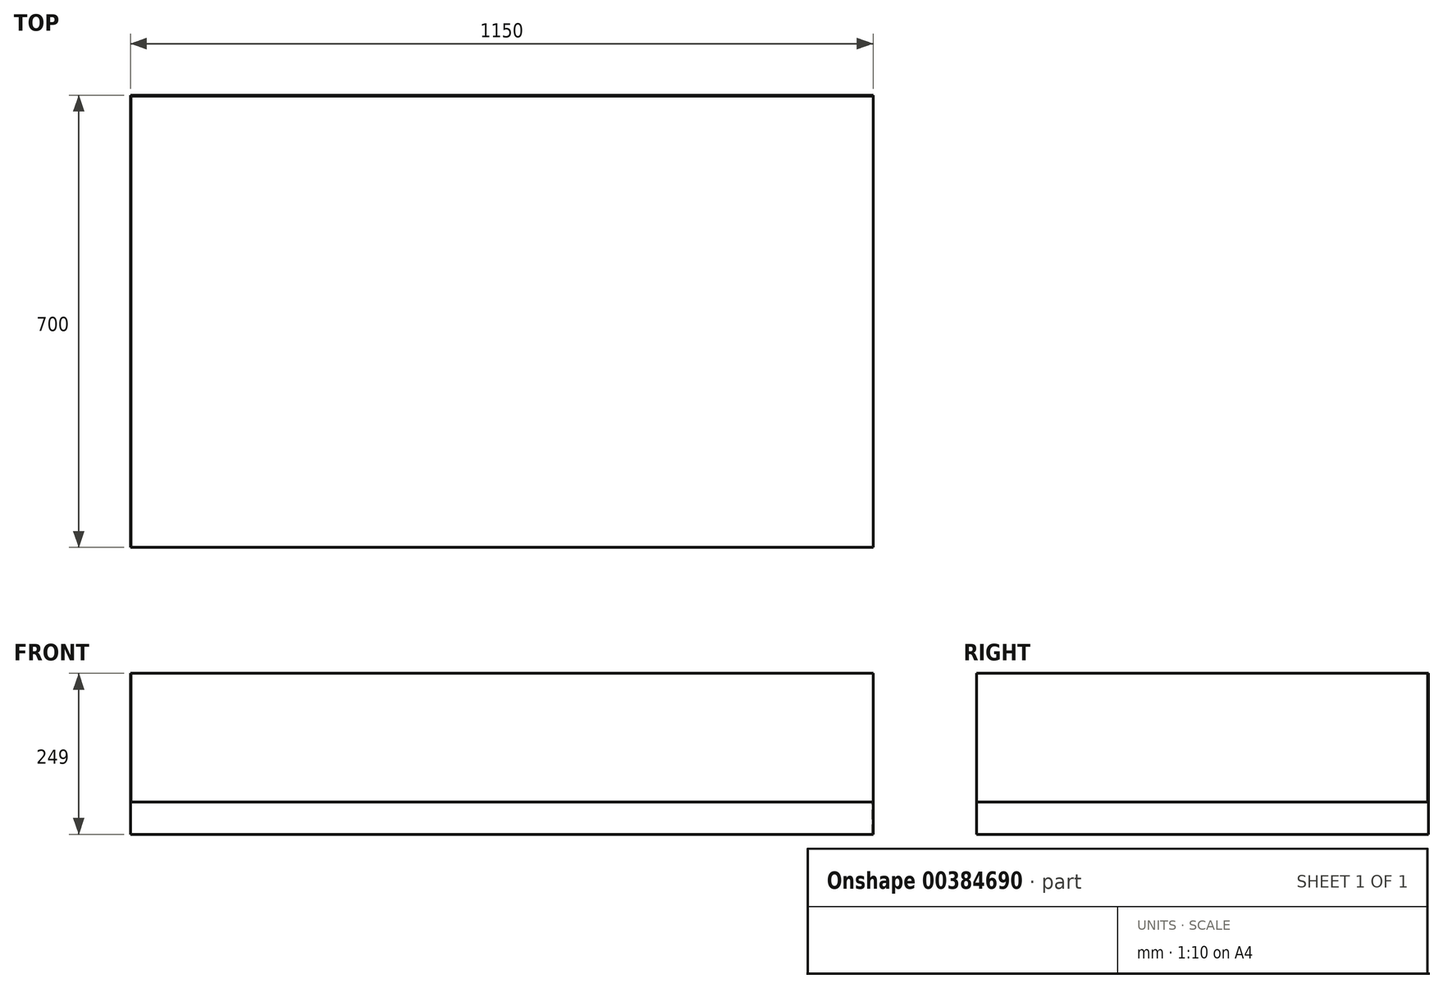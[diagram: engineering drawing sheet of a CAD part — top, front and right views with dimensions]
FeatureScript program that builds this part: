
annotation { "Feature Type Name" : "Feature", "Feature Type Description" : "" }
export const myFeature = defineFeature(function(context is Context, id is Id, definition is map)
    precondition{}
    {
        {
            var Q0;
            Q0=qCreatedBy(makeId("Right.planeOp"),FACE);
            var sketch = newSketch(context, id + "F0", { "sketchPlane" : qUnion([Q0])});
            skLineSegment(sketch, "E0", {"start": v(0, 0) * mm, "end": v(699, 0) * mm});
            skLineSegment(sketch, "E1", {"start": v(699, 0) * mm, "end": v(699, 199) * mm});
            skLineSegment(sketch, "E2", {"start": v(699, 199) * mm, "end": v(700, 199) * mm});
            skLineSegment(sketch, "E3", {"start": v(700, 199) * mm, "end": v(700, -1) * mm});
            skLineSegment(sketch, "E4", {"start": v(700, -1) * mm, "end": v(1, -1) * mm});
            skLineSegment(sketch, "E5", {"start": v(1, -1) * mm, "end": v(1, -50) * mm});
            skLineSegment(sketch, "E6", {"start": v(1, -50) * mm, "end": v(0, -50) * mm});
            skLineSegment(sketch, "E7", {"start": v(0, -50) * mm, "end": v(0, 0) * mm});
            skSolve(sketch);
        }
        {
            var Q0;
            Q0 = qSketchRegion(id + "F0", true);
            extrude(context, id + "F1", {"entities" : qUnion([Q0]), "oppositeDirection" : true, "depth" : 1150 * mm});
        }
        {
            var Q0;
            Q0=makeQuery(id+"F1.opExtrude","SWEPT_FACE",FACE,{"disambiguationData":[OSD([sQuery(id+"F0.wireOp",EDGE,"E5")])]});
            var sketch = newSketch(context, id + "F2", { "sketchPlane" : qUnion([Q0])});
            skLineSegment(sketch, "E8.bottom", {"start": v(0, -50) * mm, "end": v(1, -50) * mm});
            skLineSegment(sketch, "E8.top", {"start": v(0, -1) * mm, "end": v(1, -1) * mm});
            skLineSegment(sketch, "E8.left", {"start": v(0, -50) * mm, "end": v(0, -1) * mm});
            skLineSegment(sketch, "E8.right", {"start": v(1, -50) * mm, "end": v(1, -1) * mm});
            skSolve(sketch);
        }
        {
            var Q0;
            Q0 = qSketchRegion(id + "F2", true);
            var Q1;
            Q1=makeQuery(id+"F1.opExtrude","SWEPT_FACE",FACE,{"disambiguationData":[OSD([sQuery(id+"F0.wireOp",EDGE,"E3")])]});
            extrude(context, id + "F3", {"entities" : qUnion([Q0]), "operationType" : NewBodyOperationType.ADD, "endBound" : BoundingType.UP_TO_SURFACE, "endBoundEntityFace" : qUnion([Q1]), "depth" : 25 * mm});
        }
        {
            var Q0;
            Q0=makeQuery(id+"F1.opExtrude","SWEPT_FACE",FACE,{"disambiguationData":[OSD([sQuery(id+"F0.wireOp",EDGE,"E1")])]});
            var sketch = newSketch(context, id + "F4", { "sketchPlane" : qUnion([Q0])});
            skLineSegment(sketch, "E9.bottom", {"start": v(-1150, 0) * mm, "end": v(-1149, 0) * mm});
            skLineSegment(sketch, "E9.top", {"start": v(-1150, 199) * mm, "end": v(-1149, 199) * mm});
            skLineSegment(sketch, "E9.left", {"start": v(-1150, 0) * mm, "end": v(-1150, 199) * mm});
            skLineSegment(sketch, "E9.right", {"start": v(-1149, 0) * mm, "end": v(-1149, 199) * mm});
            skSolve(sketch);
        }
        {
            var Q0;
            Q0 = qSketchRegion(id + "F4", true);
            var Q1;
            Q1=makeQuery(id+"F1.opExtrude","SWEPT_FACE",FACE,{"disambiguationData":[OSD([sQuery(id+"F0.wireOp",EDGE,"E0")])]});
            extrude(context, id + "F5", {"entities" : qUnion([Q0]), "operationType" : NewBodyOperationType.ADD, "endBoundEntityFace" : qUnion([Q1]), "depth" : 699 * mm});
        }
    });
